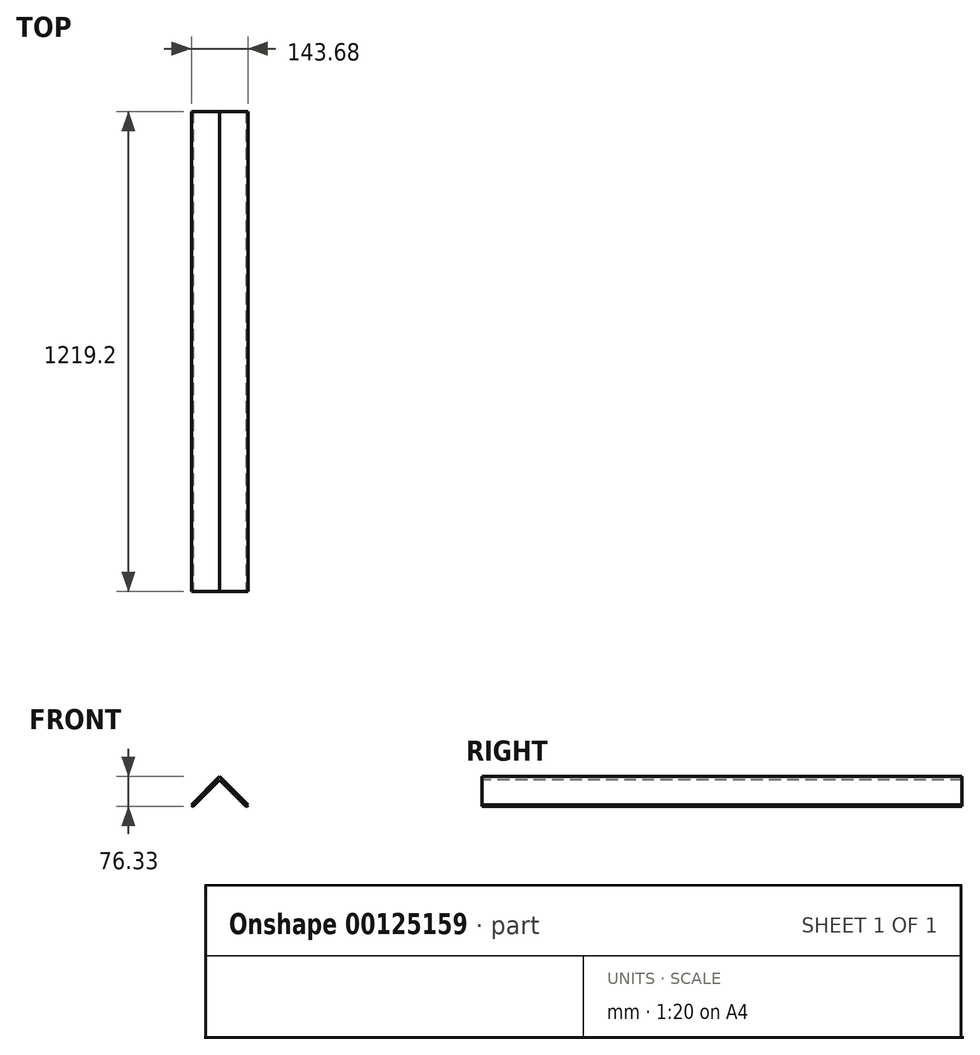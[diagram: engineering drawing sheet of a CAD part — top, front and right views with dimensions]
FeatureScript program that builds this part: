
annotation { "Feature Type Name" : "Feature", "Feature Type Description" : "" }
export const myFeature = defineFeature(function(context is Context, id is Id, definition is map)
    precondition{}
    {
        {
            var Q0;
            Q0=qCreatedBy(makeId("Front.planeOp"),FACE);
            var sketch = newSketch(context, id + "F0", { "sketchPlane" : qUnion([Q0])});
            skLineSegment(sketch, "E0", {"start": v(0, 0) * mm, "end": v(71.84, 71.84) * mm});
            skLineSegment(sketch, "E1", {"start": v(71.84, 71.84) * mm, "end": v(143.68, 0) * mm});
            skLineSegment(sketch, "E2.0", {"start": v(71.84, 62.86) * mm, "end": v(139.2, -4.5) * mm});
            skLineSegment(sketch, "E2.1", {"start": v(4.5, -4.5) * mm, "end": v(71.84, 62.86) * mm});
            skLineSegment(sketch, "E3", {"start": v(4.5, -4.5) * mm, "end": v(2.9, -4.5) * mm});
            skLineSegment(sketch, "E4", {"start": v(139.2, -4.5) * mm, "end": v(140.78, -4.5) * mm});
            skLineSegment(sketch, "E5", {"start": v(140.78, -4.5) * mm, "end": v(143.68, 0) * mm});
            skLineSegment(sketch, "E6", {"start": v(2.9, -4.5) * mm, "end": v(0, 0) * mm});
            skSolve(sketch);
        }
        {
            var Q0;
            Q0=qSketchRegion(id+"F0",true);
            extrude(context, id + "F1", {"entities" : qUnion([Q0]), "oppositeDirection" : true, "depth" : 1219.2 * mm});
        }
    });
